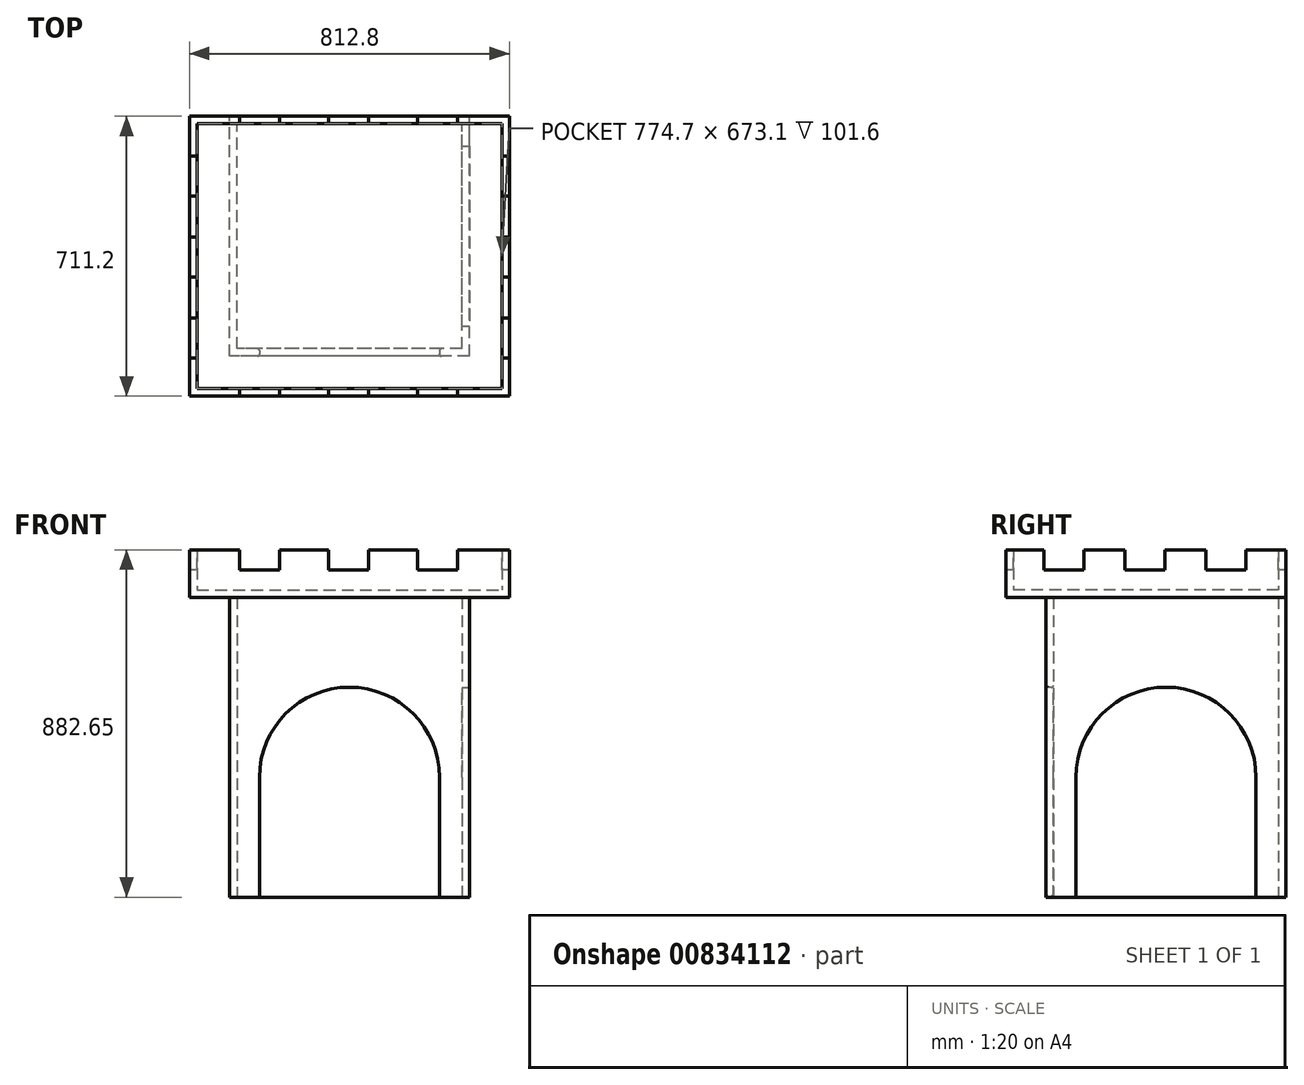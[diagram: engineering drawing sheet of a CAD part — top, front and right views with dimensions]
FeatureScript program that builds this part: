
annotation { "Feature Type Name" : "Feature", "Feature Type Description" : "" }
export const myFeature = defineFeature(function(context is Context, id is Id, definition is map)
    precondition{}
    {
        {
            var Q0;
            Q0=qCreatedBy(makeId("Top.planeOp"),FACE);
            var sketch = newSketch(context, id + "F0", { "sketchPlane" : qUnion([Q0])});
            skLineSegment(sketch, "E0.bottom", {"start": v(304.8, -304.8) * mm, "end": v(-304.8, -304.8) * mm});
            skLineSegment(sketch, "E0.top", {"start": v(304.8, 304.8) * mm, "end": v(-304.8, 304.8) * mm});
            skLineSegment(sketch, "E0.left", {"start": v(304.8, -304.8) * mm, "end": v(304.8, 304.8) * mm});
            skLineSegment(sketch, "E0.right", {"start": v(-304.8, -304.8) * mm, "end": v(-304.8, 304.8) * mm});
            skPoint(sketch, "E0.middle", {"position": v(0, 0) * mm});
            skLineSegment(sketch, "E1.bottom", {"start": v(285.75, -285.75) * mm, "end": v(-285.75, -285.75) * mm});
            skLineSegment(sketch, "E1.top", {"start": v(285.75, 285.75) * mm, "end": v(-285.75, 285.75) * mm});
            skLineSegment(sketch, "E1.left", {"start": v(285.75, -285.75) * mm, "end": v(285.75, 285.75) * mm});
            skLineSegment(sketch, "E1.right", {"start": v(-285.75, -285.75) * mm, "end": v(-285.75, 285.75) * mm});
            skSolve(sketch);
        }
        {
            var Q0;
            Q0=qSketchRegion(id+"F0",true);
            extrude(context, id + "F1", {"entities" : qUnion([Q0]), "endBound" : BoundingType.SYMMETRIC, "depth" : 762 * mm});
        }
        {
            var Q0;
            Q0=makeQuery(id+"F1.opExtrude","SWEPT_FACE",FACE,{"disambiguationData":[OSD([sQuery(id+"F0.wireOp",EDGE,"E0.bottom")])]});
            var sketch = newSketch(context, id + "F2", { "sketchPlane" : qUnion([Q0])});
            skLineSegment(sketch, "E2.bottom", {"start": v(-228.6, -381) * mm, "end": v(228.6, -381) * mm});
            skLineSegment(sketch, "E2.top", {"start": v(-228.6, -76.2) * mm, "end": v(228.6, -76.2) * mm, "construction": true});
            skLineSegment(sketch, "E2.left", {"start": v(-228.6, -381) * mm, "end": v(-228.6, -76.2) * mm});
            skLineSegment(sketch, "E2.right", {"start": v(228.6, -381) * mm, "end": v(228.6, -76.2) * mm});
            skLineSegment(sketch, "E3", {"start": v(-304.8, -381) * mm, "end": v(-228.6, -381) * mm, "construction": true});
            skLineSegment(sketch, "E4", {"start": v(228.6, -381) * mm, "end": v(304.8, -381) * mm, "construction": true});
            skArc(sketch, "E5", {"start": v(228.6, -76.2) * mm, "mid": v(0, 152.4) * mm, "end": v(-228.6, -76.2) * mm});
            skSolve(sketch);
        }
        {
            var Q0;
            Q0=qSketchRegion(id+"F2",true);
            extrude(context, id + "F3", {"entities" : qUnion([Q0]), "operationType" : NewBodyOperationType.REMOVE, "oppositeDirection" : true, "depth" : 25.4 * mm});
        }
        {
            var Q0;
            Q0=makeQuery(id+"F1.opExtrude","SWEPT_FACE",FACE,{"disambiguationData":[OSD([sQuery(id+"F0.wireOp",EDGE,"E0.left")])]});
            var sketch = newSketch(context, id + "F4", { "sketchPlane" : qUnion([Q0])});
            skLineSegment(sketch, "E6.bottom", {"start": v(-228.6, -381) * mm, "end": v(228.6, -381) * mm});
            skLineSegment(sketch, "E6.top", {"start": v(-228.6, -76.2) * mm, "end": v(228.6, -76.2) * mm, "construction": true});
            skLineSegment(sketch, "E6.left", {"start": v(-228.6, -381) * mm, "end": v(-228.6, -76.2) * mm});
            skLineSegment(sketch, "E6.right", {"start": v(228.6, -381) * mm, "end": v(228.6, -76.2) * mm});
            skLineSegment(sketch, "E7", {"start": v(-228.6, -381) * mm, "end": v(-304.8, -381) * mm, "construction": true});
            skLineSegment(sketch, "E8", {"start": v(228.6, -381) * mm, "end": v(304.8, -381) * mm, "construction": true});
            skArc(sketch, "E9", {"start": v(228.6, -76.2) * mm, "mid": v(0, 152.4) * mm, "end": v(-228.6, -76.2) * mm});
            skSolve(sketch);
        }
        {
            var Q0;
            Q0=qSketchRegion(id+"F4",true);
            extrude(context, id + "F5", {"entities" : qUnion([Q0]), "operationType" : NewBodyOperationType.REMOVE, "oppositeDirection" : true, "depth" : 25.4 * mm});
        }
        {
            var Q0;
            Q0=makeQuery(id+"F3.boolean.opBoolean","COPY",FACE,{"derivedFrom":makeQuery(id+"F3.opExtrude","SWEPT_FACE",FACE,{"disambiguationData":[OSD([sQuery(id+"F2.wireOp",EDGE,"E2.left")])]})});
            var Q1;
            Q1=makeQuery(id+"F3.boolean.opBoolean","COPY",FACE,{"derivedFrom":makeQuery(id+"F3.opExtrude","SWEPT_FACE",FACE,{"disambiguationData":[OSD([sQuery(id+"F2.wireOp",EDGE,"E5")])]})});
            var Q2;
            Q2=makeQuery(id+"F3.boolean.opBoolean","COPY",FACE,{"derivedFrom":makeQuery(id+"F3.opExtrude","SWEPT_FACE",FACE,{"disambiguationData":[OSD([sQuery(id+"F2.wireOp",EDGE,"E2.right")])]})});
            fillet(context, id + "F6", {"entities" : qUnion([Q0, Q1, Q2]), "radius" : 5.08 * mm, "tangentPropagation" : true, "allowEdgeOverflow" : false});
        }
        {
            var Q0;
            Q0=makeQuery(id+"F1.opExtrude","CAP_FACE",FACE,{"disambiguationData":[OSD([sQuery(id+"F0.wireOp",EDGE,"E0.bottom"),sQuery(id+"F0.wireOp",EDGE,"E0.top"),sQuery(id+"F0.wireOp",EDGE,"E0.left"),sQuery(id+"F0.wireOp",EDGE,"E0.right"),sQuery(id+"F0.wireOp",EDGE,"E1.bottom"),sQuery(id+"F0.wireOp",EDGE,"E1.top"),sQuery(id+"F0.wireOp",EDGE,"E1.left"),sQuery(id+"F0.wireOp",EDGE,"E1.right")])],"isStart":false});
            var sketch = newSketch(context, id + "F7", { "sketchPlane" : qUnion([Q0])});
            skLineSegment(sketch, "E10.bottom", {"start": v(-406.4, 304.8) * mm, "end": v(406.4, 304.8) * mm});
            skLineSegment(sketch, "E10.top", {"start": v(-406.4, -406.4) * mm, "end": v(406.4, -406.4) * mm});
            skLineSegment(sketch, "E10.left", {"start": v(-406.4, 304.8) * mm, "end": v(-406.4, -406.4) * mm});
            skLineSegment(sketch, "E10.right", {"start": v(406.4, 304.8) * mm, "end": v(406.4, -406.4) * mm});
            skPoint(sketch, "E11", {"position": v(0, 304.8) * mm});
            skSolve(sketch);
        }
        {
            var Q0;
            Q0=qSketchRegion(id+"F7",true);
            extrude(context, id + "F8", {"entities" : qUnion([Q0]), "operationType" : NewBodyOperationType.ADD, "depth" : 19.05 * mm});
        }
        {
            var Q0;
            Q0=makeQuery(id+"F8.opExtrude","CAP_FACE",FACE,{"disambiguationData":[OSD([sQuery(id+"F7.wireOp",EDGE,"E10.bottom"),sQuery(id+"F7.wireOp",EDGE,"E10.top"),sQuery(id+"F7.wireOp",EDGE,"E10.left"),sQuery(id+"F7.wireOp",EDGE,"E10.right")])],"isStart":false});
            var sketch = newSketch(context, id + "F9", { "sketchPlane" : qUnion([Q0])});
            skLineSegment(sketch, "E12.bottom", {"start": v(-406.4, 304.8) * mm, "end": v(406.4, 304.8) * mm});
            skLineSegment(sketch, "E12.top", {"start": v(-406.4, -406.4) * mm, "end": v(406.4, -406.4) * mm});
            skLineSegment(sketch, "E12.left", {"start": v(-406.4, 304.8) * mm, "end": v(-406.4, -406.4) * mm});
            skLineSegment(sketch, "E12.right", {"start": v(406.4, 304.8) * mm, "end": v(406.4, -406.4) * mm});
            skLineSegment(sketch, "E13.bottom", {"start": v(-387.35, 285.75) * mm, "end": v(387.35, 285.75) * mm});
            skLineSegment(sketch, "E13.top", {"start": v(-387.35, -387.35) * mm, "end": v(387.35, -387.35) * mm});
            skLineSegment(sketch, "E13.left", {"start": v(-387.35, 285.75) * mm, "end": v(-387.35, -387.35) * mm});
            skLineSegment(sketch, "E13.right", {"start": v(387.35, 285.75) * mm, "end": v(387.35, -387.35) * mm});
            skSolve(sketch);
        }
        {
            var Q0;
            Q0=qSketchRegion(id+"F9",true);
            extrude(context, id + "F10", {"entities" : qUnion([Q0]), "operationType" : NewBodyOperationType.ADD, "depth" : 101.6 * mm});
        }
        {
            var Q0;
            Q0=makeQuery(id+"F10.boolean.opBoolean","MERGE",FACE,{"derivedFrom":[makeQuery(id+"F8.opExtrude","SWEPT_FACE",FACE,{"disambiguationData":[OSD([sQuery(id+"F7.wireOp",EDGE,"E10.top")])]}),makeQuery(id+"F10.opExtrude","SWEPT_FACE",FACE,{"disambiguationData":[OSD([sQuery(id+"F9.wireOp",EDGE,"E12.top")])]})]});
            var sketch = newSketch(context, id + "F11", { "sketchPlane" : qUnion([Q0])});
            skLineSegment(sketch, "E14", {"start": v(-406.4, 501.65) * mm, "end": v(-279.4, 501.65) * mm, "construction": true});
            skLineSegment(sketch, "E15.bottom", {"start": v(-279.4, 501.65) * mm, "end": v(-177.8, 501.65) * mm});
            skLineSegment(sketch, "E15.top", {"start": v(-279.4, 450.85) * mm, "end": v(-177.8, 450.85) * mm});
            skLineSegment(sketch, "E15.left", {"start": v(-279.4, 501.65) * mm, "end": v(-279.4, 450.85) * mm});
            skLineSegment(sketch, "E15.right", {"start": v(-177.8, 501.65) * mm, "end": v(-177.8, 450.85) * mm});
            skLineSegment(sketch, "E16.1.0.0", {"start": v(-180.34, 501.65) * mm, "end": v(-53.34, 501.65) * mm, "construction": true});
            skLineSegment(sketch, "E16.1.0.1", {"start": v(-53.34, 501.65) * mm, "end": v(48.26, 501.65) * mm});
            skLineSegment(sketch, "E16.1.0.2", {"start": v(-53.34, 450.85) * mm, "end": v(48.26, 450.85) * mm});
            skLineSegment(sketch, "E16.1.0.3", {"start": v(-53.34, 501.65) * mm, "end": v(-53.34, 450.85) * mm});
            skLineSegment(sketch, "E16.1.0.4", {"start": v(48.26, 501.65) * mm, "end": v(48.26, 450.85) * mm});
            skLineSegment(sketch, "E16.2.0.0", {"start": v(45.72, 501.65) * mm, "end": v(172.72, 501.65) * mm, "construction": true});
            skLineSegment(sketch, "E16.2.0.1", {"start": v(172.72, 501.65) * mm, "end": v(274.32, 501.65) * mm});
            skLineSegment(sketch, "E16.2.0.2", {"start": v(172.72, 450.85) * mm, "end": v(274.32, 450.85) * mm});
            skLineSegment(sketch, "E16.2.0.3", {"start": v(172.72, 501.65) * mm, "end": v(172.72, 450.85) * mm});
            skLineSegment(sketch, "E16.2.0.4", {"start": v(274.32, 501.65) * mm, "end": v(274.32, 450.85) * mm});
            skLineSegment(sketch, "E16.direction1", {"start": v(-406.4, 501.65) * mm, "end": v(-180.34, 501.65) * mm, "construction": true});
            skSolve(sketch);
        }
        {
            var Q0;
            Q0=qSketchRegion(id+"F11",true);
            extrude(context, id + "F12", {"entities" : qUnion([Q0]), "operationType" : NewBodyOperationType.REMOVE, "endBound" : BoundingType.THROUGH_ALL, "oppositeDirection" : true, "depth" : 25.4 * mm});
        }
        {
            var Q0;
            Q0=makeQuery(id+"F10.boolean.opBoolean","MERGE",FACE,{"derivedFrom":[makeQuery(id+"F8.opExtrude","SWEPT_FACE",FACE,{"disambiguationData":[OSD([sQuery(id+"F7.wireOp",EDGE,"E10.left")])]}),makeQuery(id+"F10.opExtrude","SWEPT_FACE",FACE,{"disambiguationData":[OSD([sQuery(id+"F9.wireOp",EDGE,"E12.left")])]})]});
            var sketch = newSketch(context, id + "F13", { "sketchPlane" : qUnion([Q0])});
            skLineSegment(sketch, "E17", {"start": v(-304.8, 501.65) * mm, "end": v(-203.2, 501.65) * mm, "construction": true});
            skLineSegment(sketch, "E18.bottom", {"start": v(-203.2, 501.65) * mm, "end": v(-101.6, 501.65) * mm});
            skLineSegment(sketch, "E18.top", {"start": v(-203.2, 450.85) * mm, "end": v(-101.6, 450.85) * mm});
            skLineSegment(sketch, "E18.left", {"start": v(-203.2, 501.65) * mm, "end": v(-203.2, 450.85) * mm});
            skLineSegment(sketch, "E18.right", {"start": v(-101.6, 501.65) * mm, "end": v(-101.6, 450.85) * mm});
            skLineSegment(sketch, "E19.1.0.0", {"start": v(-99.06, 501.65) * mm, "end": v(2.54, 501.65) * mm, "construction": true});
            skLineSegment(sketch, "E19.1.0.1", {"start": v(2.54, 501.65) * mm, "end": v(104.14, 501.65) * mm});
            skLineSegment(sketch, "E19.1.0.2", {"start": v(2.54, 450.85) * mm, "end": v(104.14, 450.85) * mm});
            skLineSegment(sketch, "E19.1.0.3", {"start": v(2.54, 501.65) * mm, "end": v(2.54, 450.85) * mm});
            skLineSegment(sketch, "E19.1.0.4", {"start": v(104.14, 501.65) * mm, "end": v(104.14, 450.85) * mm});
            skLineSegment(sketch, "E19.2.0.0", {"start": v(106.68, 501.65) * mm, "end": v(208.28, 501.65) * mm, "construction": true});
            skLineSegment(sketch, "E19.2.0.1", {"start": v(208.28, 501.65) * mm, "end": v(309.88, 501.65) * mm});
            skLineSegment(sketch, "E19.2.0.2", {"start": v(208.28, 450.85) * mm, "end": v(309.88, 450.85) * mm});
            skLineSegment(sketch, "E19.2.0.3", {"start": v(208.28, 501.65) * mm, "end": v(208.28, 450.85) * mm});
            skLineSegment(sketch, "E19.2.0.4", {"start": v(309.88, 501.65) * mm, "end": v(309.88, 450.85) * mm});
            skLineSegment(sketch, "E19.direction1", {"start": v(-304.8, 501.65) * mm, "end": v(-99.06, 501.65) * mm, "construction": true});
            skSolve(sketch);
        }
        {
            var Q0;
            Q0=qSketchRegion(id+"F13",true);
            extrude(context, id + "F14", {"entities" : qUnion([Q0]), "operationType" : NewBodyOperationType.REMOVE, "endBound" : BoundingType.THROUGH_ALL, "oppositeDirection" : true, "depth" : 25.4 * mm});
        }
    });
